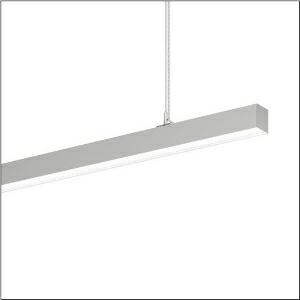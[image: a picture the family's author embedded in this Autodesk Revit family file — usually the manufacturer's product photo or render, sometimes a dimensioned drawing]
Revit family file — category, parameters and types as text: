
# Revit family: silica_21_51mx33da37sb
name_source: partatom
category: Lighting Fixtures
units: mm (PartAtom-declared; Revit-internal decimal feet)

## family parameters
Cut with Voids When Loaded = No
Host = Face
Light Source = No
Part Type = Normal
Room Calculation Point = No
Round Connector Dimension = Use Diameter
Shared = No

## types (1)
- --- (1 x LED, 5910 lm, 41.3 W, 3000K)
    Apparent Load = 41 VA
    CIE Flux Codes = 78 96 99 55 100
    Color Rendering = 80
    Color Temperature = 3000K
    Default Elevation = 1800 mm
    Description = Silica 21, office luminaire, primary optical cover: prismatic diffuser, of PMMA, CAT 2 (L<= 3000cd/m²), light emission: direct/indirect distribution, primary light characteristic: symmetric, installation type: suspended mounting, LED, rated luminous flux: 5.910lm, luminous efficacy: 143lm/W, light colour: 830, colour temperature: 3000K, control gear: DALI 2, with terminal, 3+2-pole, max. 2.5mm², mains connection: 220..240V, AC, 50/60Hz, rated input power: 41.3W, luminaire housing, of aluminium, metallic grey (RAL 9006), length: 1.204mm, width: 53mm, height: 53mm, protection rating (complete): IP20, insulation class (complete): insulation class I (protective earthing), certification: CE, permissible operating ambient temperature: 0..+35°C, standard: EN 50419, packaging unit: 1 piece
    Height = 53 mm
    Lamp = 1 x LED
    Lamp Light Flux = 5910 lm
    Lamp Power = 41.3 W
    Lamp count = 1
    Length = 1204 mm
    Luminous efficacy = 143 lm/W
    Manufacturer = Siteco
    ModVariant = No
    Model = 51MX33DA37SB
    Mounting Place = Ceiling
    Mounting Type = Pendant
    Number of Poles = 1
    OnlyDefault = Yes
    Power Factor = 1
    Product Name = Silica 21
    Product group = office luminaire | ceiling pendant
    ProductGroupID = 903
    Protection Class = Protection class I
    Protection Degree = IP 20
    RLX_Detail_Level = 1
    RLX_Emergency_Light_Flux = 0 lm
    RLX_Emergency_Type = 0
    RLX_Emergency_Type_DB = No
    RlxData = <blob elided: 23393 chars, md5=47634f14>
    Socket = socket
    Standby Power = 0 W
    System Light Flux = 5910 lm
    System Power = 41 W
    Type Comments = factory setting: luminous flux: 100 % | dim-lin: 254 | 345 mA
    Type Image = l_1335864.jpg
    URL = http://relux.com
    VarID = @adj_118713
    Voltage = 0 V
    Weight = 0.00 kg
    Width = 53 mm

## geometry (parser evidence)
native form markers: Blend x4, Sweep x13
no freeform markers — native parametric forms only
